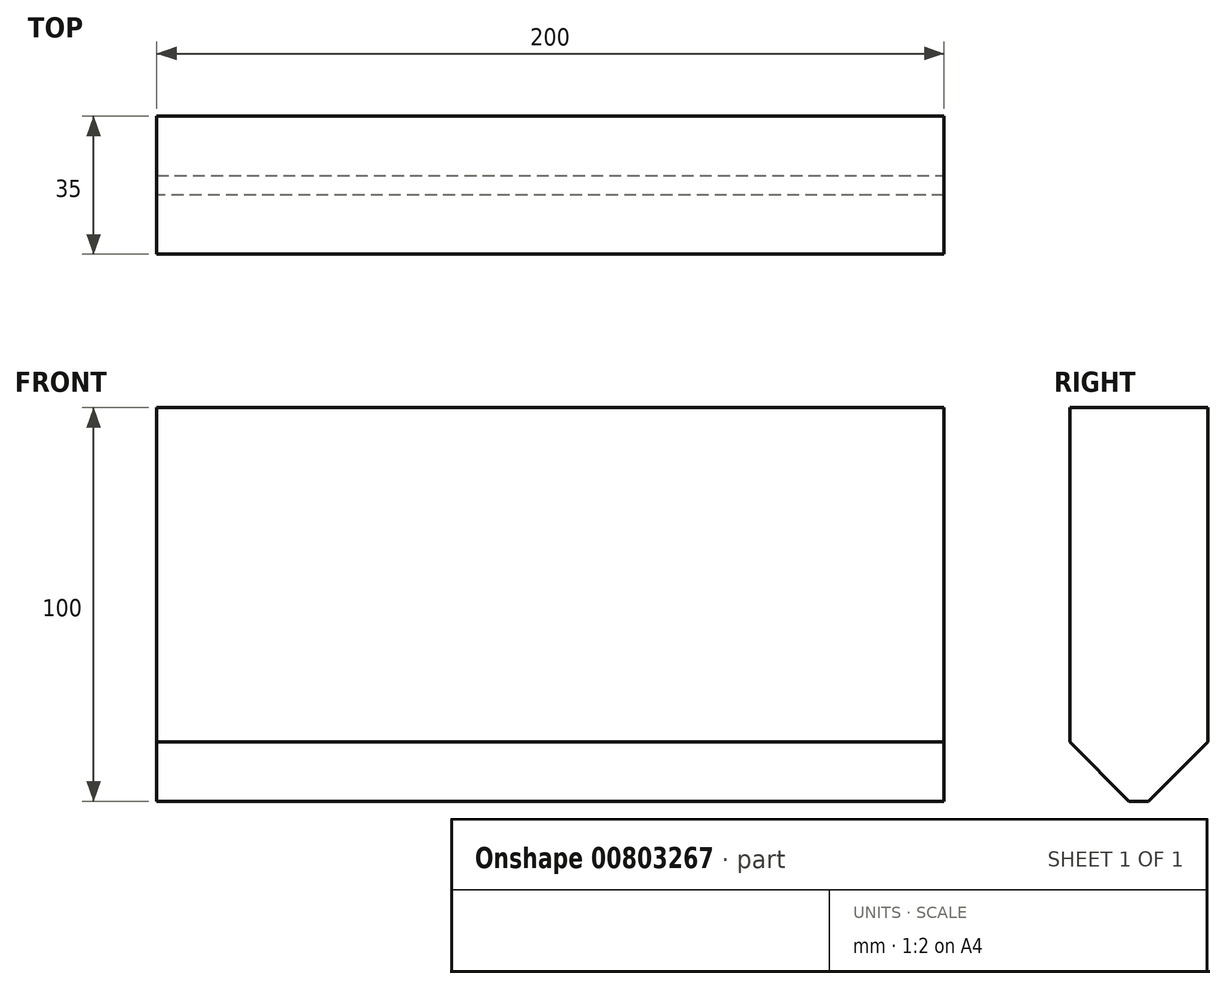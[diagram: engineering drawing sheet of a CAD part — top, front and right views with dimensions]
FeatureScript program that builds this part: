
annotation { "Feature Type Name" : "Feature", "Feature Type Description" : "" }
export const myFeature = defineFeature(function(context is Context, id is Id, definition is map)
    precondition{}
    {
        {
            var Q0;
            Q0=qCreatedBy(makeId("Right.planeOp"),FACE);
            var sketch = newSketch(context, id + "F0", { "sketchPlane" : qUnion([Q0])});
            skLineSegment(sketch, "E0.bottom", {"start": v(17.5, 50) * mm, "end": v(-17.5, 50) * mm});
            skLineSegment(sketch, "E0.top", {"start": v(17.5, -50) * mm, "end": v(-17.5, -50) * mm});
            skLineSegment(sketch, "E0.left", {"start": v(17.5, 50) * mm, "end": v(17.5, -50) * mm});
            skLineSegment(sketch, "E0.right", {"start": v(-17.5, 50) * mm, "end": v(-17.5, -50) * mm});
            skPoint(sketch, "E0.middle", {"position": v(0, 0) * mm});
            skSolve(sketch);
        }
        {
            var Q0;
            Q0=makeQuery(id+"F0.imprint","IMPRINT",FACE,{"disambiguationData":[TD([[makeQuery(id+"F0.imprint","IMPRINT",EDGE,{"derivedFrom":sQuery(id+"F0.wireOp",EDGE,"E0.bottom")}),1.0]])]});
            extrude(context, id + "F1", {"entities" : qUnion([Q0]), "endBound" : BoundingType.SYMMETRIC, "depth" : 200 * mm, "offsetDistance" : 25 * mm});
        }
        {
            var Q0;
            Q0=makeQuery(id+"F1.opExtrude","SWEPT_EDGE",EDGE,{"disambiguationData":[OSD([sQuery(id+"F0.wireOp",EDGE,"E0.top"),sQuery(id+"F0.wireOp",EDGE,"E0.right")])]});
            var Q1;
            Q1=makeQuery(id+"F1.opExtrude","SWEPT_EDGE",EDGE,{"disambiguationData":[OSD([sQuery(id+"F0.wireOp",EDGE,"E0.top"),sQuery(id+"F0.wireOp",EDGE,"E0.left")])]});
            chamfer(context, id + "F2", {"entities" : qUnion([Q0, Q1]), "width" : 15 * mm, "tangentPropagation" : true});
        }
    });
